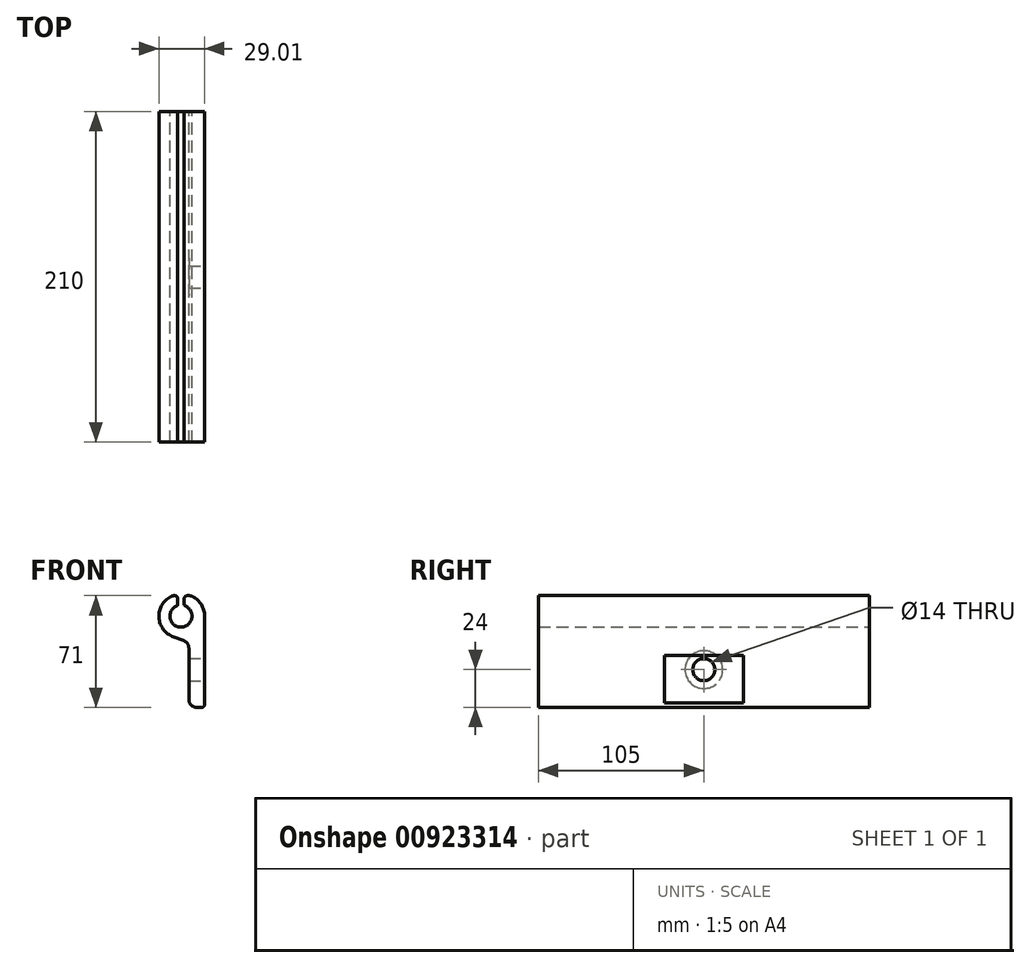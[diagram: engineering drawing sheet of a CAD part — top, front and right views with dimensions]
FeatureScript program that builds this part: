
annotation { "Feature Type Name" : "Feature", "Feature Type Description" : "" }
export const myFeature = defineFeature(function(context is Context, id is Id, definition is map)
    precondition{}
    {
        {
            var Q0;
            Q0=qCreatedBy(makeId("Front.planeOp"),FACE);
            var sketch = newSketch(context, id + "F0", { "sketchPlane" : qUnion([Q0])});
            skArc(sketch, "E0", {"start": v(4.5, -30.5) * mm, "mid": v(5.96, -34.04) * mm, "end": v(9.5, -35.5) * mm});
            skLineSegment(sketch, "E1", {"start": v(9.5, -35.5) * mm, "end": v(12.5, -35.5) * mm});
            skArc(sketch, "E2", {"start": v(12.5, -35.5) * mm, "mid": v(13.91, -34.91) * mm, "end": v(14.5, -33.5) * mm});
            skLineSegment(sketch, "E3", {"start": v(14.5, -33.5) * mm, "end": v(14.5, 22.5) * mm});
            skArc(sketch, "E4", {"start": v(14.5, 22.5) * mm, "mid": v(12.45, 29.79) * mm, "end": v(6.91, 34.94) * mm});
            skArc(sketch, "E5", {"start": v(6.91, 34.94) * mm, "mid": v(5.8, 35.36) * mm, "end": v(4.62, 35.5) * mm});
            skLineSegment(sketch, "E6", {"start": v(4.62, 35.5) * mm, "end": v(3.5, 35.5) * mm});
            skArc(sketch, "E7", {"start": v(3.5, 35.5) * mm, "mid": v(2.09, 34.91) * mm, "end": v(1.5, 33.5) * mm});
            skLineSegment(sketch, "E8", {"start": v(1.5, 33.5) * mm, "end": v(1.5, 30.25) * mm});
            skArc(sketch, "E9", {"start": v(1.5, 30.25) * mm, "mid": v(1.74, 29.43) * mm, "end": v(2.38, 28.88) * mm});
            skArc(sketch, "E10", {"start": v(-3.38, 28.88) * mm, "mid": v(-0.5, 15.5) * mm, "end": v(2.38, 28.88) * mm});
            skArc(sketch, "E11", {"start": v(-3.38, 28.88) * mm, "mid": v(-2.74, 29.43) * mm, "end": v(-2.5, 30.25) * mm});
            skLineSegment(sketch, "E12", {"start": v(-2.5, 30.25) * mm, "end": v(-2.5, 33.5) * mm});
            skArc(sketch, "E13", {"start": v(-2.5, 33.5) * mm, "mid": v(-3.09, 34.91) * mm, "end": v(-4.5, 35.5) * mm});
            skLineSegment(sketch, "E14", {"start": v(-4.5, 35.5) * mm, "end": v(-4.62, 35.5) * mm});
            skArc(sketch, "E15", {"start": v(-4.62, 35.5) * mm, "mid": v(-5.8, 35.36) * mm, "end": v(-6.91, 34.94) * mm});
            skArc(sketch, "E16", {"start": v(-6.91, 34.94) * mm, "mid": v(-14.47, 21.61) * mm, "end": v(-5.29, 9.34) * mm});
            skLineSegment(sketch, "E17", {"start": v(-5.29, 9.34) * mm, "end": v(1.21, 6.98) * mm});
            skArc(sketch, "E18", {"start": v(4.5, 2.28) * mm, "mid": v(3.6, 5.15) * mm, "end": v(1.21, 6.98) * mm});
            skLineSegment(sketch, "E19", {"start": v(4.5, 2.28) * mm, "end": v(4.5, -30.5) * mm});
            skLineSegment(sketch, "E20", {"start": v(4.5, -23.5) * mm, "end": v(4.4, -23.5) * mm});
            skLineSegment(sketch, "E21", {"start": v(4.4, -23.5) * mm, "end": v(4.4, 0.5) * mm});
            skLineSegment(sketch, "E22", {"start": v(4.4, 0.5) * mm, "end": v(4.5, 0.5) * mm});
            skSolve(sketch);
        }
        {
            var Q0;
            {var subQ0=sQuery(id+"F0.wireOp",EDGE,"E0");Q0=makeQuery(id+"F0.imprint","IMPRINT",FACE,{"disambiguationData":[TD([[makeQuery(id+"F0.imprint","IMPRINT",EDGE,{"derivedFrom":subQ0}),1.0]])]});}
            extrude(context, id + "F1", {"entities" : qUnion([Q0]), "endBound" : BoundingType.SYMMETRIC, "depth" : 210 * mm, "offsetDistance" : 25 * mm});
        }
        {
            var Q0;
            Q0=makeQuery(id+"F1.opExtrude","SWEPT_FACE",FACE,{"disambiguationData":[OSD([sQuery(id+"F0.wireOp",EDGE,"E19")])]});
            var sketch = newSketch(context, id + "F2", { "sketchPlane" : qUnion([Q0])});
            skCircle(sketch, "E23", {"center": v(0, -11.5) * mm, "radius": 12 * mm});
            skCircle(sketch, "E24", {"center": v(0, -11.5) * mm, "radius": 7 * mm});
            skSolve(sketch);
        }
        {
            var Q0;
            Q0=makeQuery(id+"F2.imprint","IMPRINT",FACE,{"disambiguationData":[TD([[makeQuery(id+"F2.imprint","IMPRINT",EDGE,{"derivedFrom":sQuery(id+"F2.wireOp",EDGE,"E23")}),1.0]])]});
            extrude(context, id + "F3", {"entities" : qUnion([Q0]), "operationType" : NewBodyOperationType.ADD, "depth" : 0.01 * mm, "offsetDistance" : 25 * mm});
        }
        {
            var Q0;
            Q0=makeQuery(id+"F1.opExtrude","SWEPT_FACE",FACE,{"disambiguationData":[OSD([sQuery(id+"F0.wireOp",EDGE,"E3")])]});
            var sketch = newSketch(context, id + "F4", { "sketchPlane" : qUnion([Q0])});
            skLineSegment(sketch, "E25.bottom", {"start": v(25, -2.5) * mm, "end": v(-25, -2.5) * mm});
            skLineSegment(sketch, "E25.top", {"start": v(25, -32.5) * mm, "end": v(-25, -32.5) * mm});
            skLineSegment(sketch, "E25.left", {"start": v(25, -2.5) * mm, "end": v(25, -32.5) * mm});
            skLineSegment(sketch, "E25.right", {"start": v(-25, -2.5) * mm, "end": v(-25, -32.5) * mm});
            skPoint(sketch, "E25.middle", {"position": v(0, -17.5) * mm});
            skPoint(sketch, "E25.middle.positionSnap0", {"position": v(0, -33.5) * mm});
            skPoint(sketch, "E25.centerSnap0", {"position": v(0, -33.5) * mm});
            skSolve(sketch);
        }
        {
            var Q0;
            Q0=makeQuery(id+"F4.imprint","IMPRINT",FACE,{"disambiguationData":[TD([[makeQuery(id+"F4.imprint","IMPRINT",EDGE,{"derivedFrom":sQuery(id+"F4.wireOp",EDGE,"E25.bottom")}),1.0]])]});
            extrude(context, id + "F5", {"entities" : qUnion([Q0]), "operationType" : NewBodyOperationType.ADD, "depth" : 0.01 * mm, "offsetDistance" : 25 * mm});
        }
        {
            var Q0;
            Q0=makeQuery(id+"F3.boolean.opBoolean","SPLIT",FACE,{"disambiguationData":[TD([makeQuery(id+"F3.opExtrude","SWEPT_FACE",FACE,{"disambiguationData":[OSD([sQuery(id+"F2.wireOp",EDGE,"E24")])]})])],"derivedFrom":makeQuery(id+"F1.opExtrude","SWEPT_FACE",FACE,{"disambiguationData":[OSD([sQuery(id+"F0.wireOp",EDGE,"E19")])]})});
            extrude(context, id + "F6", {"entities" : qUnion([Q0]), "operationType" : NewBodyOperationType.REMOVE, "depth" : -20 * mm, "offsetDistance" : 25 * mm});
        }
    });
